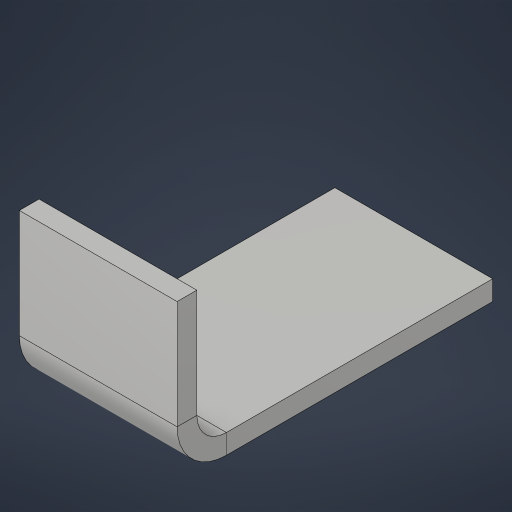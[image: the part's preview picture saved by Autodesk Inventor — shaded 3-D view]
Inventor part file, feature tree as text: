
AUTODESK INVENTOR PART (.ipt)
format: ipt  version: 2023.1 (Build 271208000, 208)  size: 194,048 bytes
history: native  units: in
note: dims shown in document units (in); Inventor stores cm internally (conversion verified against a paired STEP export)
features: sheet_metal_op x4, sketch x2, other x2
ambient origin geometry x8: Origin, YZ Plane, XZ Plane, XY Plane, X Axis, Y Axis, Z Axis, Center Point
bodies: Solid1 (feature_tree)
feature tree (8):
  sheet_metal_op  "Face1"
  sheet_metal_op  "Flange1"
  sketch  "Sketch1"  dims[d0=1.0in]
  other  "Plate1"
  sketch  "Sketch2"  dims[d1=2.0in d2=0.125in d3=0.125in d4=0.0625in d5=0.25in d6=0.1875in d7=1.0in d8=90.0deg d9=0.1875in d10=0.5in d11=0.125in d12=0.1875in]
  other  "Plate2"
  sheet_metal_op  "Bend1"
  sheet_metal_op  "Corner1"
